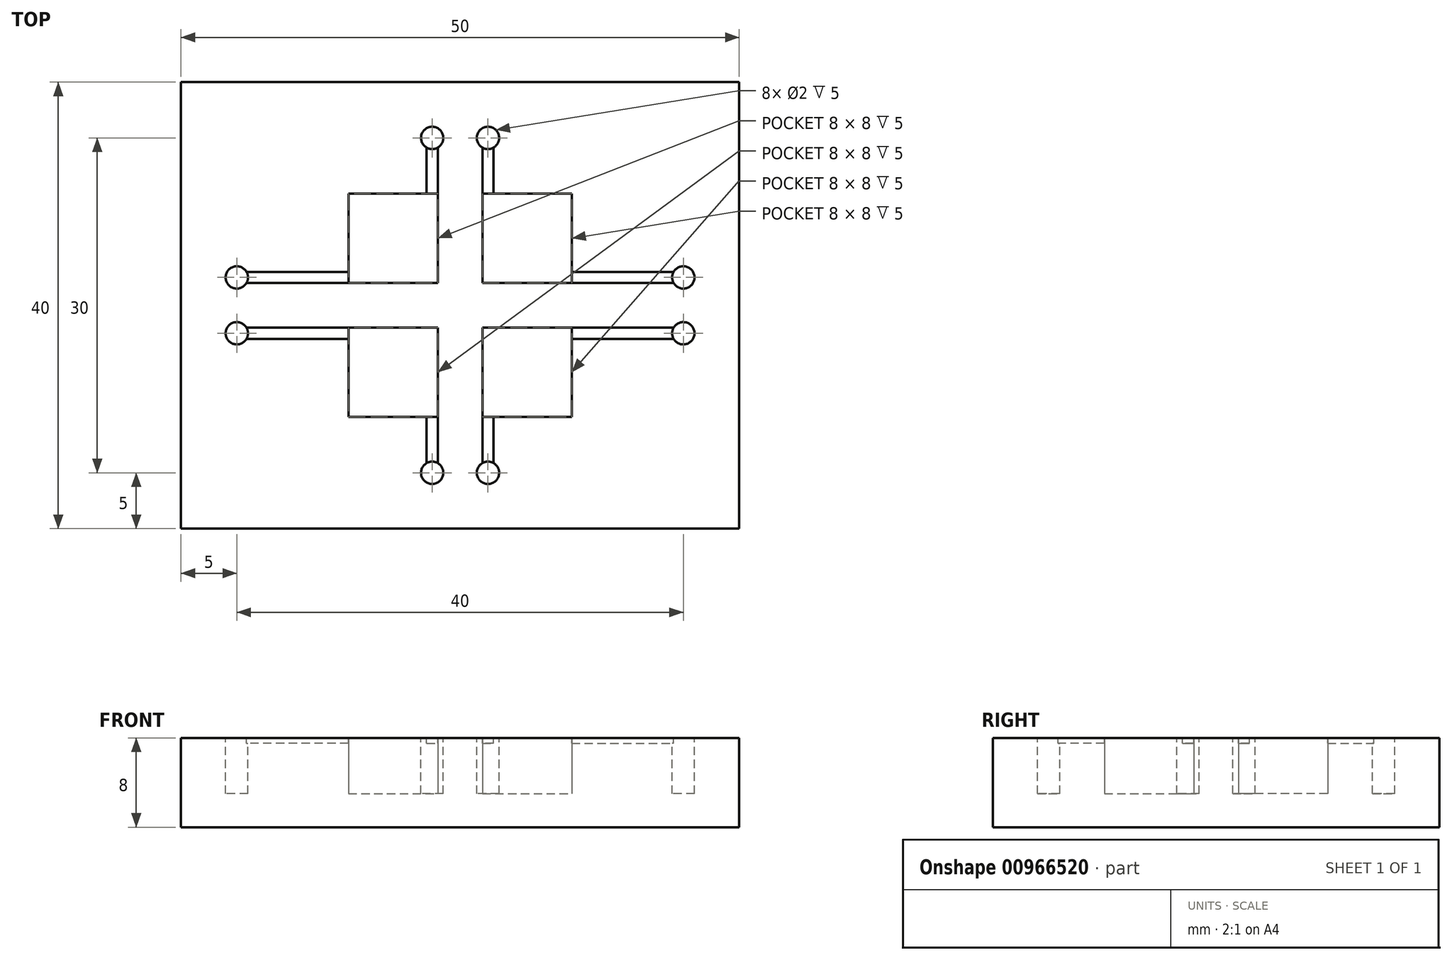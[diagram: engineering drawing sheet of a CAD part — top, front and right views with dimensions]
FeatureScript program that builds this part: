
annotation { "Feature Type Name" : "Feature", "Feature Type Description" : "" }
export const myFeature = defineFeature(function(context is Context, id is Id, definition is map)
    precondition{}
    {
        {
            var Q0;
            Q0=qCreatedBy(makeId("Top.planeOp"),FACE);
            var sketch = newSketch(context, id + "F0", { "sketchPlane" : qUnion([Q0])});
            skLineSegment(sketch, "E0.bottom", {"start": v(25, -20) * mm, "end": v(-25, -20) * mm});
            skLineSegment(sketch, "E0.top", {"start": v(25, 20) * mm, "end": v(-25, 20) * mm});
            skLineSegment(sketch, "E0.left", {"start": v(25, -20) * mm, "end": v(25, 20) * mm});
            skLineSegment(sketch, "E0.right", {"start": v(-25, -20) * mm, "end": v(-25, 20) * mm});
            skPoint(sketch, "E0.middle", {"position": v(0, 0) * mm});
            skLineSegment(sketch, "E1", {"start": v(-25, 20) * mm, "end": v(-10, 20) * mm});
            skLineSegment(sketch, "E2", {"start": v(-10, 20) * mm, "end": v(-10, 10) * mm, "construction": true});
            skLineSegment(sketch, "E3.bottom", {"start": v(-10, 10) * mm, "end": v(-2, 10) * mm});
            skLineSegment(sketch, "E3.top", {"start": v(-10, 2) * mm, "end": v(-2, 2) * mm});
            skLineSegment(sketch, "E3.left", {"start": v(-10, 10) * mm, "end": v(-10, 2) * mm});
            skLineSegment(sketch, "E3.right", {"start": v(-2, 10) * mm, "end": v(-2, 2) * mm});
            skLineSegment(sketch, "E4.1.0.0", {"start": v(2, 10) * mm, "end": v(10, 10) * mm});
            skLineSegment(sketch, "E4.1.0.1", {"start": v(10, 10) * mm, "end": v(10, 2) * mm});
            skLineSegment(sketch, "E4.1.0.2", {"start": v(2, 10) * mm, "end": v(2, 2) * mm});
            skLineSegment(sketch, "E4.1.0.3", {"start": v(2, 2) * mm, "end": v(10, 2) * mm});
            skLineSegment(sketch, "E4.direction1", {"start": v(-10, 2) * mm, "end": v(2, 2) * mm, "construction": true});
            skLineSegment(sketch, "E5.MirrorCS", {"start": v(2, -2) * mm, "end": v(10, -2) * mm});
            skLineSegment(sketch, "E6.MirrorCS", {"start": v(10, -10) * mm, "end": v(10, -2) * mm});
            skLineSegment(sketch, "E7.MirrorCS", {"start": v(2, -10) * mm, "end": v(2, -2) * mm});
            skLineSegment(sketch, "E8.MirrorCS", {"start": v(2, -10) * mm, "end": v(10, -10) * mm});
            skLineSegment(sketch, "E9.MirrorCS", {"start": v(-2, -10) * mm, "end": v(-2, -2) * mm});
            skLineSegment(sketch, "E10.MirrorCS", {"start": v(-10, -10) * mm, "end": v(-10, -2) * mm});
            skLineSegment(sketch, "E11.MirrorCS", {"start": v(-10, -10) * mm, "end": v(-2, -10) * mm});
            skLineSegment(sketch, "E12", {"start": v(-10, -2) * mm, "end": v(-2, -2) * mm});
            skSolve(sketch);
        }
        {
            var Q0;
            Q0 = qSketchRegion(id + "F0", true);
            extrude(context, id + "F1", {"entities" : qUnion([Q0]), "depth" : 5 * mm, "offsetDistance" : 25 * mm});
        }
        {
            var Q0;
            Q0=makeQuery(id+"F1.opExtrude","CAP_FACE",FACE,{"disambiguationData":[OSD([sQuery(id+"F0.wireOp",EDGE,"E0.bottom"),sQuery(id+"F0.wireOp",EDGE,"E0.top"),sQuery(id+"F0.wireOp",EDGE,"E0.left"),sQuery(id+"F0.wireOp",EDGE,"E0.right"),sQuery(id+"F0.wireOp",EDGE,"E1"),sQuery(id+"F0.wireOp",EDGE,"E3.bottom"),sQuery(id+"F0.wireOp",EDGE,"E3.top"),sQuery(id+"F0.wireOp",EDGE,"E3.left"),sQuery(id+"F0.wireOp",EDGE,"E3.right"),sQuery(id+"F0.wireOp",EDGE,"E4.1.0.0"),sQuery(id+"F0.wireOp",EDGE,"E4.1.0.1"),sQuery(id+"F0.wireOp",EDGE,"E4.1.0.2"),sQuery(id+"F0.wireOp",EDGE,"E4.1.0.3"),sQuery(id+"F0.wireOp",EDGE,"E5.MirrorCS"),sQuery(id+"F0.wireOp",EDGE,"E6.MirrorCS"),sQuery(id+"F0.wireOp",EDGE,"E7.MirrorCS"),sQuery(id+"F0.wireOp",EDGE,"E8.MirrorCS"),sQuery(id+"F0.wireOp",EDGE,"E9.MirrorCS"),sQuery(id+"F0.wireOp",EDGE,"E10.MirrorCS"),sQuery(id+"F0.wireOp",EDGE,"E11.MirrorCS"),sQuery(id+"F0.wireOp",EDGE,"E12")])],"isStart":true});
            var sketch = newSketch(context, id + "F2", { "sketchPlane" : qUnion([Q0])});
            skLineSegment(sketch, "E13.bottom", {"start": v(-25, -20) * mm, "end": v(25, -20) * mm});
            skLineSegment(sketch, "E13.top", {"start": v(-25, 20) * mm, "end": v(25, 20) * mm});
            skLineSegment(sketch, "E13.left", {"start": v(-25, -20) * mm, "end": v(-25, 20) * mm});
            skLineSegment(sketch, "E13.right", {"start": v(25, -20) * mm, "end": v(25, 20) * mm});
            skPoint(sketch, "E13.middle", {"position": v(0, 0) * mm});
            skSolve(sketch);
        }
        {
            var Q0;
            Q0 = qSketchRegion(id + "F2", true);
            extrude(context, id + "F3", {"entities" : qUnion([Q0]), "operationType" : NewBodyOperationType.ADD, "depth" : 3 * mm, "offsetDistance" : 25 * mm});
        }
        {
            var Q0;
            Q0=makeQuery(id+"F1.opExtrude","CAP_FACE",FACE,{"disambiguationData":[OSD([sQuery(id+"F0.wireOp",EDGE,"E0.bottom"),sQuery(id+"F0.wireOp",EDGE,"E0.top"),sQuery(id+"F0.wireOp",EDGE,"E0.left"),sQuery(id+"F0.wireOp",EDGE,"E0.right"),sQuery(id+"F0.wireOp",EDGE,"E1"),sQuery(id+"F0.wireOp",EDGE,"E3.bottom"),sQuery(id+"F0.wireOp",EDGE,"E3.top"),sQuery(id+"F0.wireOp",EDGE,"E3.left"),sQuery(id+"F0.wireOp",EDGE,"E3.right"),sQuery(id+"F0.wireOp",EDGE,"E4.1.0.0"),sQuery(id+"F0.wireOp",EDGE,"E4.1.0.1"),sQuery(id+"F0.wireOp",EDGE,"E4.1.0.2"),sQuery(id+"F0.wireOp",EDGE,"E4.1.0.3"),sQuery(id+"F0.wireOp",EDGE,"E5.MirrorCS"),sQuery(id+"F0.wireOp",EDGE,"E6.MirrorCS"),sQuery(id+"F0.wireOp",EDGE,"E7.MirrorCS"),sQuery(id+"F0.wireOp",EDGE,"E8.MirrorCS"),sQuery(id+"F0.wireOp",EDGE,"E9.MirrorCS"),sQuery(id+"F0.wireOp",EDGE,"E10.MirrorCS"),sQuery(id+"F0.wireOp",EDGE,"E11.MirrorCS"),sQuery(id+"F0.wireOp",EDGE,"E12")])],"isStart":false});
            var sketch = newSketch(context, id + "F4", { "sketchPlane" : qUnion([Q0])});
            skLineSegment(sketch, "E14.bottom", {"start": v(2, -10) * mm, "end": v(3, -10) * mm});
            skLineSegment(sketch, "E14.top", {"start": v(2, -15) * mm, "end": v(3, -15) * mm});
            skLineSegment(sketch, "E14.left", {"start": v(2, -10) * mm, "end": v(2, -15) * mm});
            skLineSegment(sketch, "E14.right", {"start": v(3, -10) * mm, "end": v(3, -15) * mm});
            skLineSegment(sketch, "E15.MirrorCS", {"start": v(-2, -10) * mm, "end": v(-2, -15) * mm});
            skLineSegment(sketch, "E16.MirrorCS", {"start": v(-3, -10) * mm, "end": v(-3, -15) * mm});
            skLineSegment(sketch, "E17.MirrorCS", {"start": v(-2, -10) * mm, "end": v(-3, -10) * mm});
            skLineSegment(sketch, "E18.MirrorCS", {"start": v(-2, -15) * mm, "end": v(-3, -15) * mm});
            skLineSegment(sketch, "E19.MirrorCS", {"start": v(-2, 10) * mm, "end": v(-3, 10) * mm});
            skLineSegment(sketch, "E20.MirrorCS", {"start": v(-3, 10) * mm, "end": v(-3, 15) * mm});
            skLineSegment(sketch, "E21.MirrorCS", {"start": v(-2, 15) * mm, "end": v(-3, 15) * mm});
            skLineSegment(sketch, "E22.MirrorCS", {"start": v(-2, 10) * mm, "end": v(-2, 15) * mm});
            skLineSegment(sketch, "E23.MirrorCS", {"start": v(2, 10) * mm, "end": v(2, 15) * mm});
            skLineSegment(sketch, "E24.MirrorCS", {"start": v(2, 10) * mm, "end": v(3, 10) * mm});
            skLineSegment(sketch, "E25.MirrorCS", {"start": v(3, 10) * mm, "end": v(3, 15) * mm});
            skLineSegment(sketch, "E26.MirrorCS", {"start": v(2, 15) * mm, "end": v(3, 15) * mm});
            skLineSegment(sketch, "E27.bottom", {"start": v(10, -2) * mm, "end": v(20, -2) * mm});
            skLineSegment(sketch, "E27.top", {"start": v(10, -3) * mm, "end": v(20, -3) * mm});
            skLineSegment(sketch, "E27.left", {"start": v(10, -2) * mm, "end": v(10, -3) * mm});
            skLineSegment(sketch, "E27.right", {"start": v(20, -2) * mm, "end": v(20, -3) * mm});
            skLineSegment(sketch, "E28.MirrorCS", {"start": v(10, 2) * mm, "end": v(20, 2) * mm});
            skLineSegment(sketch, "E29.MirrorCS", {"start": v(10, 3) * mm, "end": v(20, 3) * mm});
            skLineSegment(sketch, "E30.MirrorCS", {"start": v(20, 2) * mm, "end": v(20, 3) * mm});
            skLineSegment(sketch, "E31.MirrorCS", {"start": v(10, 2) * mm, "end": v(10, 3) * mm});
            skLineSegment(sketch, "E32.MirrorCS", {"start": v(-10, 3) * mm, "end": v(-20, 3) * mm});
            skLineSegment(sketch, "E33.MirrorCS", {"start": v(-10, 2) * mm, "end": v(-20, 2) * mm});
            skLineSegment(sketch, "E34.MirrorCS", {"start": v(-10, -2) * mm, "end": v(-20, -2) * mm});
            skLineSegment(sketch, "E35.MirrorCS", {"start": v(-10, -3) * mm, "end": v(-20, -3) * mm});
            skLineSegment(sketch, "E36.MirrorCS", {"start": v(-10, -2) * mm, "end": v(-10, -3) * mm});
            skLineSegment(sketch, "E37.MirrorCS", {"start": v(-20, -2) * mm, "end": v(-20, -3) * mm});
            skLineSegment(sketch, "E38.MirrorCS", {"start": v(-20, 2) * mm, "end": v(-20, 3) * mm});
            skLineSegment(sketch, "E39.MirrorCS", {"start": v(-10, 2) * mm, "end": v(-10, 3) * mm});
            skSolve(sketch);
        }
        {
            var Q0;
            Q0 = qSketchRegion(id + "F4", true);
            extrude(context, id + "F5", {"entities" : qUnion([Q0]), "operationType" : NewBodyOperationType.REMOVE, "oppositeDirection" : true, "depth" : 0.5 * mm, "offsetDistance" : 25 * mm});
        }
        {
            var Q0;
            Q0=makeQuery(id+"F1.opExtrude","CAP_FACE",FACE,{"disambiguationData":[OSD([sQuery(id+"F0.wireOp",EDGE,"E0.bottom"),sQuery(id+"F0.wireOp",EDGE,"E0.top"),sQuery(id+"F0.wireOp",EDGE,"E0.left"),sQuery(id+"F0.wireOp",EDGE,"E0.right"),sQuery(id+"F0.wireOp",EDGE,"E1"),sQuery(id+"F0.wireOp",EDGE,"E3.bottom"),sQuery(id+"F0.wireOp",EDGE,"E3.top"),sQuery(id+"F0.wireOp",EDGE,"E3.left"),sQuery(id+"F0.wireOp",EDGE,"E3.right"),sQuery(id+"F0.wireOp",EDGE,"E4.1.0.0"),sQuery(id+"F0.wireOp",EDGE,"E4.1.0.1"),sQuery(id+"F0.wireOp",EDGE,"E4.1.0.2"),sQuery(id+"F0.wireOp",EDGE,"E4.1.0.3"),sQuery(id+"F0.wireOp",EDGE,"E5.MirrorCS"),sQuery(id+"F0.wireOp",EDGE,"E6.MirrorCS"),sQuery(id+"F0.wireOp",EDGE,"E7.MirrorCS"),sQuery(id+"F0.wireOp",EDGE,"E8.MirrorCS"),sQuery(id+"F0.wireOp",EDGE,"E9.MirrorCS"),sQuery(id+"F0.wireOp",EDGE,"E10.MirrorCS"),sQuery(id+"F0.wireOp",EDGE,"E11.MirrorCS"),sQuery(id+"F0.wireOp",EDGE,"E12")])],"isStart":false});
            var sketch = newSketch(context, id + "F6", { "sketchPlane" : qUnion([Q0])});
            skCircle(sketch, "E40", {"center": v(20, -2.5) * mm, "radius": 1 * mm});
            skCircle(sketch, "E41.MirrorC", {"center": v(20, 2.5) * mm, "radius": 1 * mm});
            skCircle(sketch, "E42.MirrorC", {"center": v(-20, -2.5) * mm, "radius": 1 * mm});
            skCircle(sketch, "E43.MirrorC", {"center": v(-20, 2.5) * mm, "radius": 1 * mm});
            skCircle(sketch, "E44", {"center": v(2.5, -15) * mm, "radius": 1 * mm});
            skCircle(sketch, "E45.MirrorC", {"center": v(-2.5, -15) * mm, "radius": 1 * mm});
            skCircle(sketch, "E46.MirrorC", {"center": v(2.5, 15) * mm, "radius": 1 * mm});
            skCircle(sketch, "E47.MirrorC", {"center": v(-2.5, 15) * mm, "radius": 1 * mm});
            skSolve(sketch);
        }
        {
            var Q0;
            Q0 = qSketchRegion(id + "F6", true);
            extrude(context, id + "F7", {"entities" : qUnion([Q0]), "operationType" : NewBodyOperationType.REMOVE, "oppositeDirection" : true, "depth" : 5 * mm, "offsetDistance" : 25 * mm});
        }
    });
